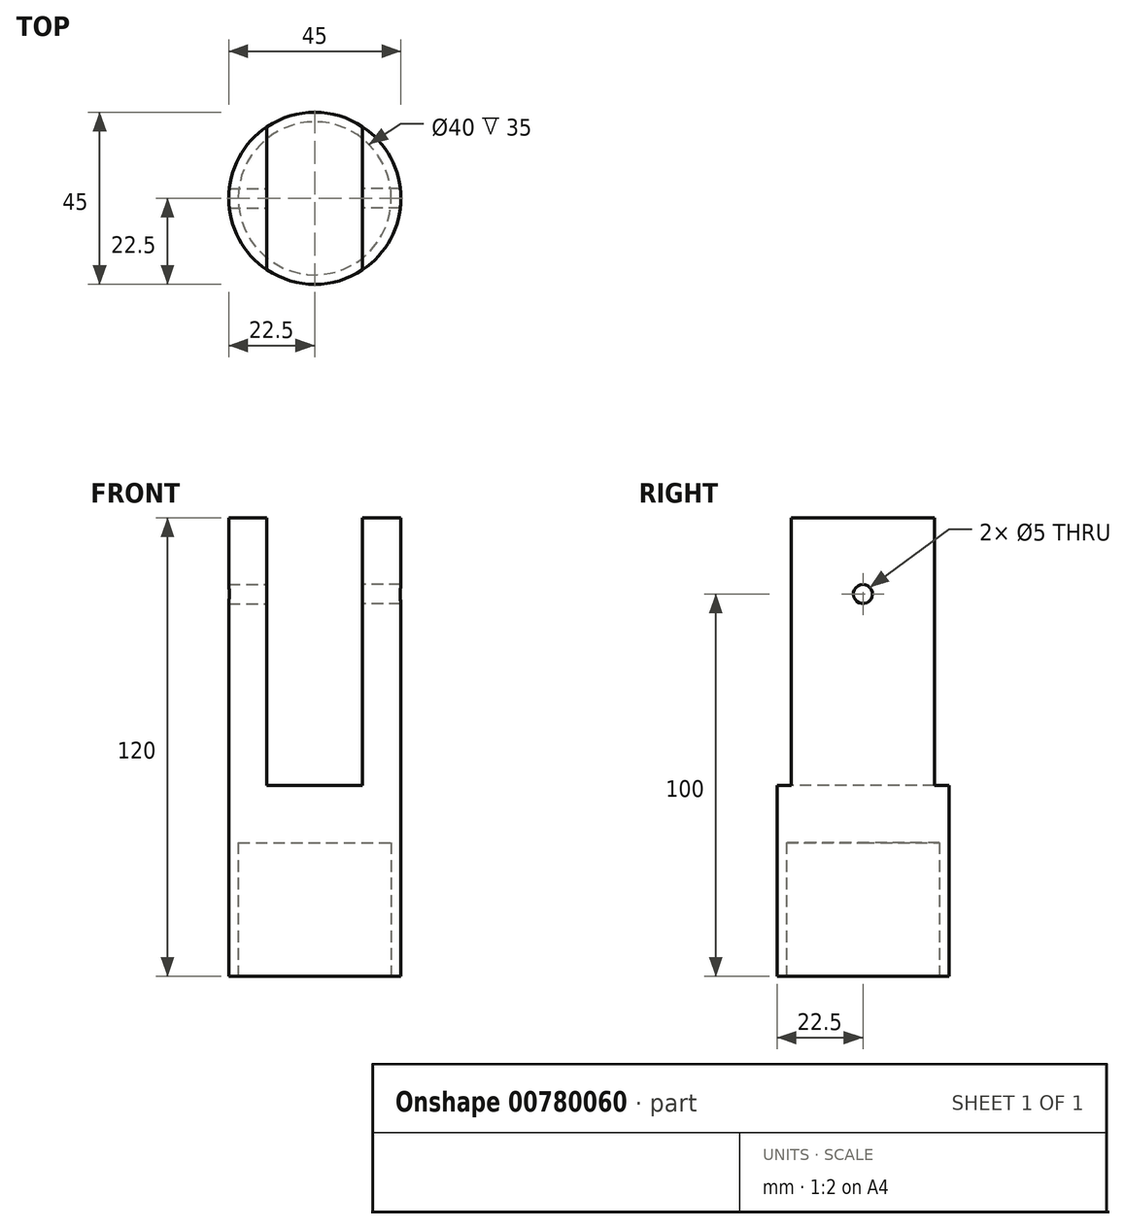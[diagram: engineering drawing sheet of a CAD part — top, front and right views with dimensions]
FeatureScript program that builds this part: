
annotation { "Feature Type Name" : "Feature", "Feature Type Description" : "" }
export const myFeature = defineFeature(function(context is Context, id is Id, definition is map)
    precondition{}
    {
        {
            var Q0;
            Q0=qCreatedBy(makeId("Top.planeOp"),FACE);
            var sketch = newSketch(context, id + "F0", { "sketchPlane" : qUnion([Q0])});
            skCircle(sketch, "E0", {"center": v(0, 0) * mm, "radius": 22.5 * mm});
            skSolve(sketch);
        }
        {
            var Q0;
            Q0=makeQuery(id+"F0.imprint","IMPRINT",FACE,{"disambiguationData":[TD([[makeQuery(id+"F0.imprint","IMPRINT",EDGE,{"derivedFrom":sQuery(id+"F0.wireOp",EDGE,"E0")}),1.0]])]});
            extrude(context, id + "F1", {"entities" : qUnion([Q0]), "depth" : 120 * mm, "offsetDistance" : 25 * mm});
        }
        {
            var Q0;
            Q0=makeQuery(id+"F1.opExtrude","CAP_FACE",FACE,{"disambiguationData":[OSD([sQuery(id+"F0.wireOp",EDGE,"E0")])],"isStart":false});
            var sketch = newSketch(context, id + "F2", { "sketchPlane" : qUnion([Q0])});
            skLineSegment(sketch, "E1", {"start": v(-12.5, 18.7) * mm, "end": v(-12.5, -18.7) * mm});
            skLineSegment(sketch, "E2", {"start": v(12.5, 18.7) * mm, "end": v(12.5, -18.7) * mm});
            skSolve(sketch);
        }
        {
            var Q0;
            {var subQ0=sQuery(id+"F2.wireOp",EDGE,"E1");Q0=makeQuery(id+"F2.imprint","IMPRINT",FACE,{"disambiguationData":[TD([[makeQuery(id+"F2.imprint","IMPRINT",EDGE,{"derivedFrom":subQ0}),1.0]])]});}
            var Q1;
            Q1=sQuery(id+"F2.wireOp",EDGE,"E1");
            var Q2;
            Q2=sQuery(id+"F2.wireOp",EDGE,"E2");
            extrude(context, id + "F3", {"entities" : qUnion([Q0]), "operationType" : NewBodyOperationType.REMOVE, "surfaceEntities" : qUnion([Q1, Q2]), "oppositeDirection" : true, "depth" : 70 * mm, "offsetDistance" : 25 * mm});
        }
        {
            var Q0;
            Q0=makeQuery(id+"F1.opExtrude","CAP_FACE",FACE,{"disambiguationData":[OSD([sQuery(id+"F0.wireOp",EDGE,"E0")])],"isStart":true});
            var sketch = newSketch(context, id + "F4", { "sketchPlane" : qUnion([Q0])});
            skCircle(sketch, "E3", {"center": v(0, 0) * mm, "radius": 20 * mm});
            skSolve(sketch);
        }
        {
            var Q0;
            Q0=makeQuery(id+"F4.imprint","IMPRINT",FACE,{"disambiguationData":[TD([[makeQuery(id+"F4.imprint","IMPRINT",EDGE,{"derivedFrom":sQuery(id+"F4.wireOp",EDGE,"E3")}),1.0]])]});
            extrude(context, id + "F5", {"entities" : qUnion([Q0]), "operationType" : NewBodyOperationType.REMOVE, "oppositeDirection" : true, "depth" : 35 * mm, "offsetDistance" : 25 * mm});
        }
        {
            var Q0;
            Q0=qCreatedBy(makeId("Right.planeOp"),FACE);
            var sketch = newSketch(context, id + "F6", { "sketchPlane" : qUnion([Q0])});
            skPoint(sketch, "E4", {"position": v(0, 100) * mm});
            skSolve(sketch);
        }
        {
            var Q0;
            Q0=sQuery(id+"F6.wireOp",VERTEX,"E4");
            var Q1;
            Q1=makeQuery(id+"F1.opExtrude","SWEPT_BODY",BODY,{"disambiguationData":[OSD([sQuery(id+"F0.wireOp",EDGE,"E0")])]});
            hole(context, id + "F7", {"style" : HoleStyle.SIMPLE, "endStyle" : HoleEndStyle.THROUGH, "holeDiameter" : 5 * mm, "majorDiameter" : 5 * mm, "isTappedThrough" : true, "tappedDepth" : 12 * mm, "tapClearance" : 3, "locations" : qUnion([Q0]), "scope" : qUnion([Q1])});
        }
        {
            var Q0;
            Q0=qCreatedBy(makeId("Right.planeOp"),FACE);
            var sketch = newSketch(context, id + "F8", { "sketchPlane" : qUnion([Q0])});
            skPoint(sketch, "E5", {"position": v(0, 100) * mm});
            skSolve(sketch);
        }
        {
            var Q0;
            Q0=sQuery(id+"F8.wireOp",VERTEX,"E5");
            var Q1;
            Q1=makeQuery(id+"F1.opExtrude","SWEPT_BODY",BODY,{"disambiguationData":[OSD([sQuery(id+"F0.wireOp",EDGE,"E0")])]});
            hole(context, id + "F9", {"style" : HoleStyle.SIMPLE, "endStyle" : HoleEndStyle.THROUGH, "oppositeDirection" : true, "holeDiameter" : 5 * mm, "majorDiameter" : 5 * mm, "isTappedThrough" : true, "tappedDepth" : 12 * mm, "tapClearance" : 3, "locations" : qUnion([Q0]), "scope" : qUnion([Q1])});
        }
    });
